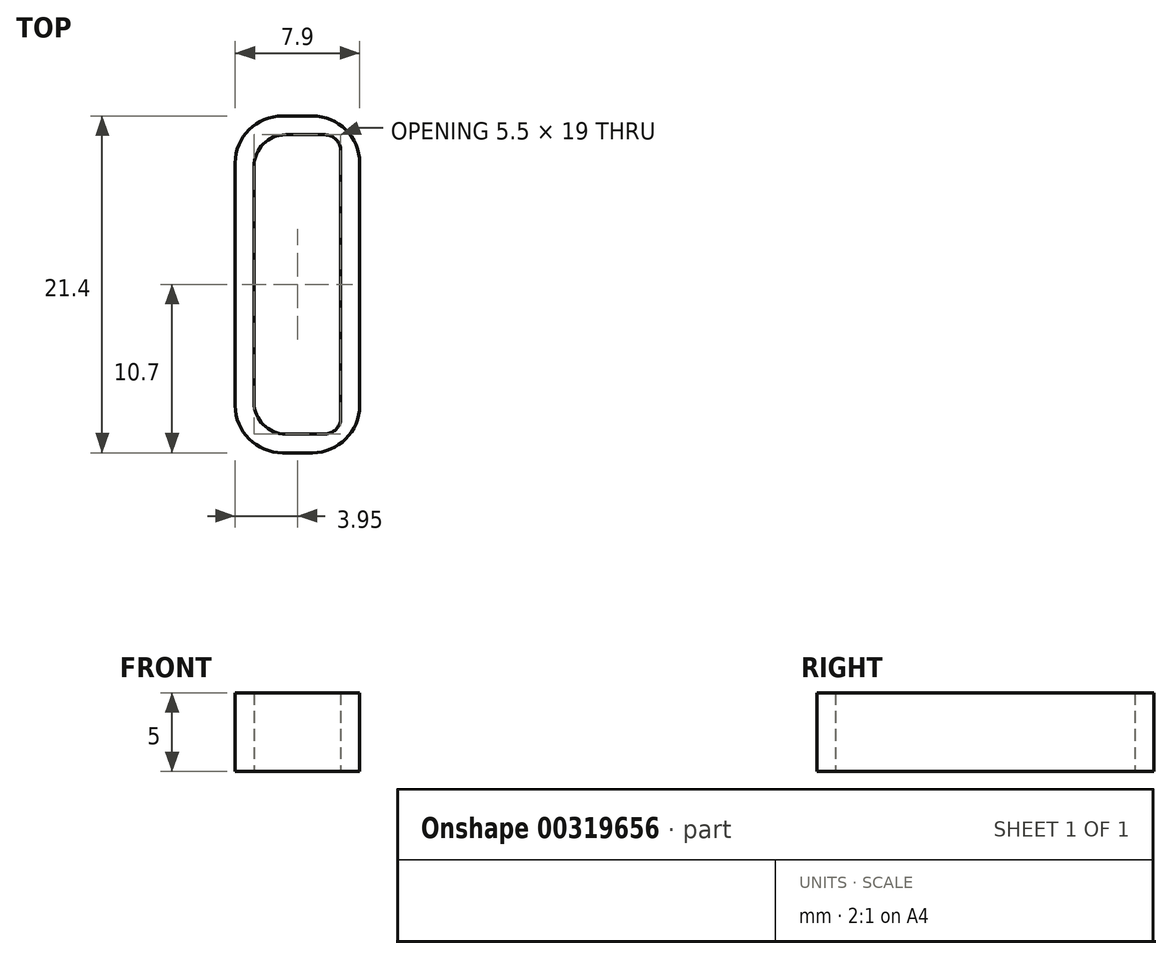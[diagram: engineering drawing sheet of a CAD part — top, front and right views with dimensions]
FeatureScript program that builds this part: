
annotation { "Feature Type Name" : "Feature", "Feature Type Description" : "" }
export const myFeature = defineFeature(function(context is Context, id is Id, definition is map)
    precondition{}
    {
        {
            var Q0;
            Q0=qCreatedBy(makeId("Top.planeOp"),FACE);
            var sketch = newSketch(context, id + "F0", { "sketchPlane" : qUnion([Q0])});
            skLineSegment(sketch, "E0.bottom", {"start": v(2, 0) * mm, "end": v(4.5, 0) * mm});
            skLineSegment(sketch, "E0.top", {"start": v(2, -19) * mm, "end": v(4.5, -19) * mm});
            skLineSegment(sketch, "E0.left", {"start": v(0, -2) * mm, "end": v(0, -17) * mm});
            skLineSegment(sketch, "E0.right", {"start": v(5.5, -1) * mm, "end": v(5.5, -18) * mm});
            skLineSegment(sketch, "E1.0", {"start": v(1.8, 1.2) * mm, "end": v(3.7, 1.2) * mm});
            skLineSegment(sketch, "E1.1", {"start": v(-1.2, -1.8) * mm, "end": v(-1.2, -17.2) * mm});
            skLineSegment(sketch, "E1.2", {"start": v(1.8, -20.2) * mm, "end": v(3.7, -20.2) * mm});
            skLineSegment(sketch, "E1.3", {"start": v(6.7, -1.8) * mm, "end": v(6.7, -17.2) * mm});
            skPoint(sketch, "E2.visualSharp", {"position": v(-1.2, 1.2) * mm});
            skArc(sketch, "E2.filletArc", {"start": v(1.8, 1.2) * mm, "mid": v(-0.32, 0.32) * mm, "end": v(-1.2, -1.8) * mm});
            skPoint(sketch, "E3.visualSharp", {"position": v(6.7, 1.2) * mm});
            skArc(sketch, "E3.filletArc", {"start": v(6.7, -1.8) * mm, "mid": v(5.82, 0.32) * mm, "end": v(3.7, 1.2) * mm});
            skPoint(sketch, "E4.visualSharp", {"position": v(6.7, -20.2) * mm});
            skArc(sketch, "E4.filletArc", {"start": v(3.7, -20.2) * mm, "mid": v(5.82, -19.32) * mm, "end": v(6.7, -17.2) * mm});
            skPoint(sketch, "E5.visualSharp", {"position": v(-1.2, -20.2) * mm});
            skArc(sketch, "E5.filletArc", {"start": v(-1.2, -17.2) * mm, "mid": v(-0.32, -19.32) * mm, "end": v(1.8, -20.2) * mm});
            skPoint(sketch, "E6.visualSharp", {"position": v(0, 0) * mm});
            skArc(sketch, "E6.filletArc", {"start": v(2, 0) * mm, "mid": v(0.59, -0.59) * mm, "end": v(0, -2) * mm});
            skPoint(sketch, "E7.visualSharp", {"position": v(5.5, 0) * mm});
            skArc(sketch, "E7.filletArc", {"start": v(5.5, -1) * mm, "mid": v(5.2, -0.3) * mm, "end": v(4.5, 0) * mm});
            skPoint(sketch, "E8.visualSharp", {"position": v(5.5, -19) * mm});
            skArc(sketch, "E8.filletArc", {"start": v(4.5, -19) * mm, "mid": v(5.2, -18.7) * mm, "end": v(5.5, -18) * mm});
            skPoint(sketch, "E9.visualSharp", {"position": v(0, -19) * mm});
            skArc(sketch, "E9.filletArc", {"start": v(0, -17) * mm, "mid": v(0.59, -18.41) * mm, "end": v(2, -19) * mm});
            skSolve(sketch);
        }
        {
            var Q0;
            Q0=makeQuery(id+"F0.imprint","IMPRINT",FACE,{"disambiguationData":[TD([[makeQuery(id+"F0.imprint","IMPRINT",EDGE,{"derivedFrom":sQuery(id+"F0.wireOp",EDGE,"E0.bottom")}),1.0]])]});
            extrude(context, id + "F1", {"entities" : qUnion([Q0]), "depth" : 5 * mm});
        }
    });
